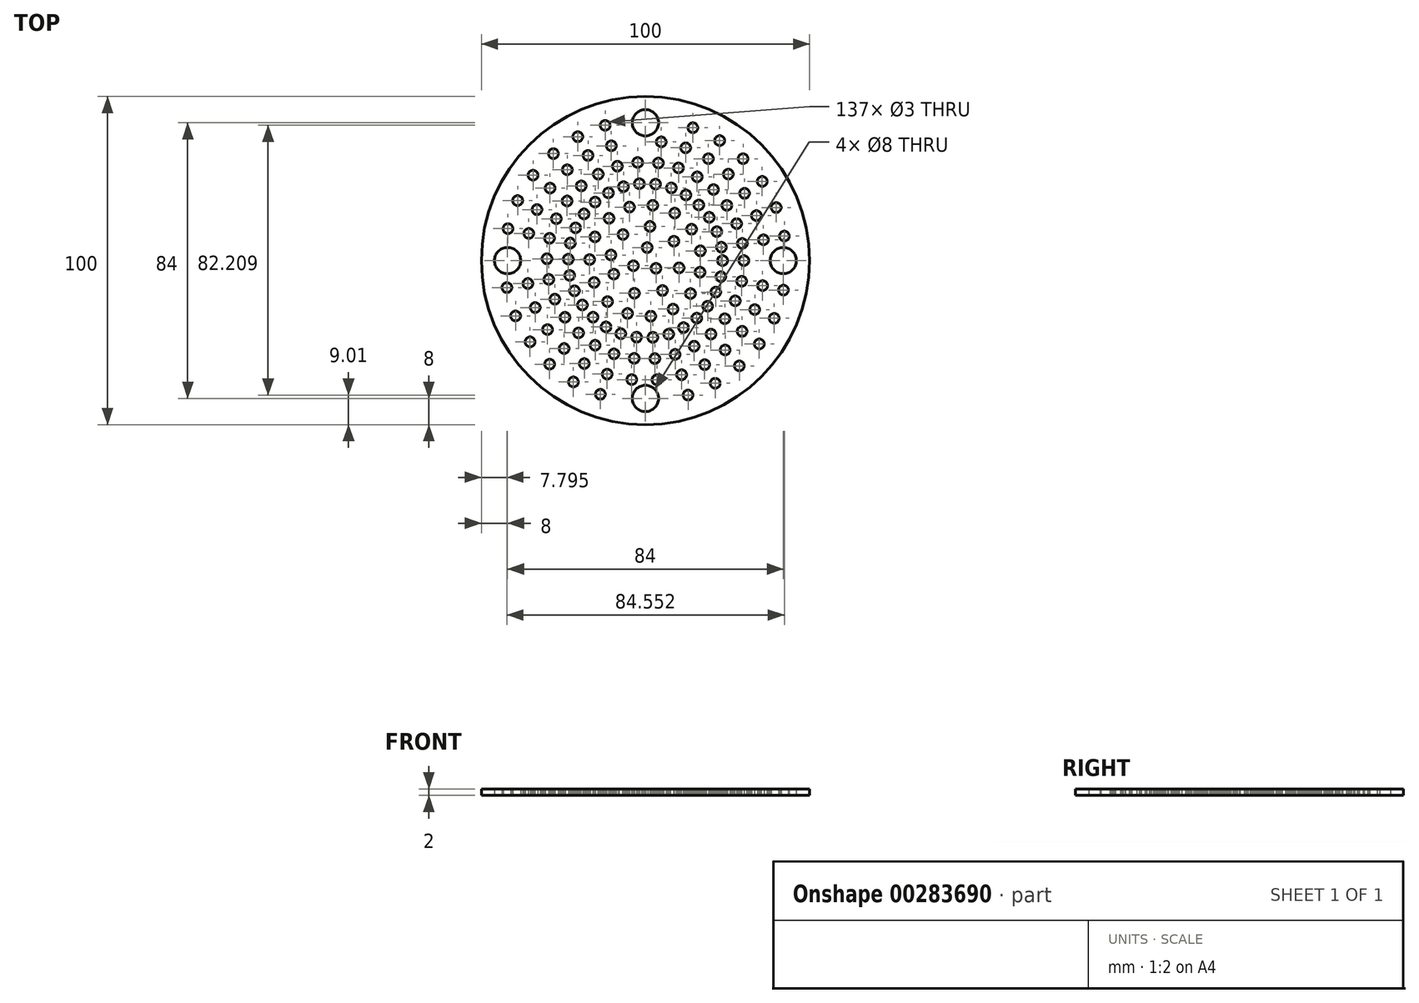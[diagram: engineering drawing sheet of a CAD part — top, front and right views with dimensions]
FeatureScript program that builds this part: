
annotation { "Feature Type Name" : "Feature", "Feature Type Description" : "" }
export const myFeature = defineFeature(function(context is Context, id is Id, definition is map)
    precondition{}
    {
        {
            var Q0;
            Q0=qCreatedBy(makeId("Top.planeOp"),FACE);
            var sketch = newSketch(context, id + "F0", { "sketchPlane" : qUnion([Q0])});
            skCircle(sketch, "E0", {"center": v(0, 0) * mm, "radius": 50 * mm});
            skCircle(sketch, "E1", {"center": v(-42, 0) * mm, "radius": 4 * mm});
            skCircle(sketch, "E2.1.0", {"center": v(0, 42) * mm, "radius": 4 * mm});
            skCircle(sketch, "E2.2.0", {"center": v(42, 0) * mm, "radius": 4 * mm});
            skCircle(sketch, "E2.3.0", {"center": v(0, -42) * mm, "radius": 4 * mm});
            skLineSegment(sketch, "E2.anchor1", {"start": v(0, 0) * mm, "end": v(-42, 0) * mm, "construction": true});
            skLineSegment(sketch, "E2.anchor2", {"start": v(0, 0) * mm, "end": v(0, -42) * mm, "construction": true});
            skCircle(sketch, "E3.3.0.0", {"center": v(23.5, 0) * mm, "radius": 1.5 * mm});
            skCircle(sketch, "E3.4.0.0", {"center": v(30, 0) * mm, "radius": 1.5 * mm});
            skLineSegment(sketch, "E3.direction1", {"start": v(4, 0) * mm, "end": v(10.5, 0) * mm, "construction": true});
            skLineSegment(sketch, "E3.direction2", {"start": v(4, 0) * mm, "end": v(4, 22) * mm, "construction": true});
            skCircle(sketch, "E4.1.0", {"center": v(35.7, -7.63) * mm, "radius": 1.5 * mm});
            skCircle(sketch, "E4.1.1", {"center": v(29.34, -6.27) * mm, "radius": 1.5 * mm});
            skCircle(sketch, "E4.1.2", {"center": v(22.98, -4.91) * mm, "radius": 1.5 * mm});
            skCircle(sketch, "E4.1.3", {"center": v(16.62, -3.55) * mm, "radius": 1.5 * mm});
            skCircle(sketch, "E4.1.4", {"center": v(10.27, -2.2) * mm, "radius": 1.5 * mm});
            skLineSegment(sketch, "E4.1.6", {"start": v(3.91, -0.84) * mm, "end": v(10.27, -2.2) * mm, "construction": true});
            skCircle(sketch, "E4.1.7", {"center": v(42.05, -9) * mm, "radius": 1.5 * mm});
            skCircle(sketch, "E4.2.0", {"center": v(33.3, -14.93) * mm, "radius": 1.5 * mm});
            skCircle(sketch, "E4.2.1", {"center": v(27.38, -12.27) * mm, "radius": 1.5 * mm});
            skCircle(sketch, "E4.2.2", {"center": v(21.45, -9.6) * mm, "radius": 1.5 * mm});
            skLineSegment(sketch, "E4.2.6", {"start": v(3.65, -1.64) * mm, "end": v(9.58, -4.3) * mm, "construction": true});
            skCircle(sketch, "E4.2.7", {"center": v(39.24, -17.58) * mm, "radius": 1.5 * mm});
            skCircle(sketch, "E4.3.0", {"center": v(29.45, -21.56) * mm, "radius": 1.5 * mm});
            skCircle(sketch, "E4.3.1", {"center": v(24.2, -17.72) * mm, "radius": 1.5 * mm});
            skCircle(sketch, "E4.3.2", {"center": v(18.96, -13.88) * mm, "radius": 1.5 * mm});
            skCircle(sketch, "E4.3.3", {"center": v(13.72, -10.04) * mm, "radius": 1.5 * mm});
            skCircle(sketch, "E4.3.5", {"center": v(3.23, -2.36) * mm, "radius": 1.5 * mm});
            skLineSegment(sketch, "E4.3.6", {"start": v(3.23, -2.36) * mm, "end": v(8.47, -6.2) * mm, "construction": true});
            skCircle(sketch, "E4.3.7", {"center": v(34.7, -25.4) * mm, "radius": 1.5 * mm});
            skCircle(sketch, "E4.4.0", {"center": v(24.3, -27.24) * mm, "radius": 1.5 * mm});
            skCircle(sketch, "E4.4.1", {"center": v(19.97, -22.4) * mm, "radius": 1.5 * mm});
            skCircle(sketch, "E4.4.2", {"center": v(15.64, -17.54) * mm, "radius": 1.5 * mm});
            skLineSegment(sketch, "E4.4.6", {"start": v(2.66, -2.99) * mm, "end": v(6.99, -7.84) * mm, "construction": true});
            skCircle(sketch, "E4.4.7", {"center": v(28.62, -32.1) * mm, "radius": 1.5 * mm});
            skCircle(sketch, "E4.5.0", {"center": v(18.06, -31.72) * mm, "radius": 1.5 * mm});
            skCircle(sketch, "E4.5.1", {"center": v(14.84, -26.07) * mm, "radius": 1.5 * mm});
            skCircle(sketch, "E4.5.2", {"center": v(11.63, -20.42) * mm, "radius": 1.5 * mm});
            skCircle(sketch, "E4.5.3", {"center": v(8.41, -14.77) * mm, "radius": 1.5 * mm});
            skCircle(sketch, "E4.5.4", {"center": v(5.2, -9.12) * mm, "radius": 1.5 * mm});
            skLineSegment(sketch, "E4.5.6", {"start": v(1.98, -3.48) * mm, "end": v(5.2, -9.12) * mm, "construction": true});
            skCircle(sketch, "E4.5.7", {"center": v(21.28, -37.37) * mm, "radius": 1.5 * mm});
            skCircle(sketch, "E4.6.0", {"center": v(11.03, -34.8) * mm, "radius": 1.5 * mm});
            skCircle(sketch, "E4.6.1", {"center": v(9.06, -28.6) * mm, "radius": 1.5 * mm});
            skCircle(sketch, "E4.6.2", {"center": v(7.1, -22.4) * mm, "radius": 1.5 * mm});
            skLineSegment(sketch, "E4.6.6", {"start": v(1.2, -3.81) * mm, "end": v(3.17, -10) * mm, "construction": true});
            skCircle(sketch, "E4.6.7", {"center": v(13, -41) * mm, "radius": 1.5 * mm});
            skCircle(sketch, "E4.7.0", {"center": v(3.5, -36.33) * mm, "radius": 1.5 * mm});
            skCircle(sketch, "E4.7.1", {"center": v(2.88, -29.86) * mm, "radius": 1.5 * mm});
            skCircle(sketch, "E4.7.2", {"center": v(2.26, -23.4) * mm, "radius": 1.5 * mm});
            skCircle(sketch, "E4.7.3", {"center": v(1.63, -16.92) * mm, "radius": 1.5 * mm});
            skLineSegment(sketch, "E4.7.6", {"start": v(0.38, -3.98) * mm, "end": v(1, -10.45) * mm, "construction": true});
            skCircle(sketch, "E4.8.0", {"center": v(-4.16, -36.26) * mm, "radius": 1.5 * mm});
            skCircle(sketch, "E4.8.1", {"center": v(-3.42, -29.8) * mm, "radius": 1.5 * mm});
            skCircle(sketch, "E4.8.2", {"center": v(-2.68, -23.35) * mm, "radius": 1.5 * mm});
            skLineSegment(sketch, "E4.8.6", {"start": v(-0.46, -3.97) * mm, "end": v(-1.2, -10.43) * mm, "construction": true});
            skCircle(sketch, "E4.9.0", {"center": v(-11.65, -34.59) * mm, "radius": 1.5 * mm});
            skCircle(sketch, "E4.9.1", {"center": v(-9.58, -28.43) * mm, "radius": 1.5 * mm});
            skCircle(sketch, "E4.9.2", {"center": v(-7.5, -22.27) * mm, "radius": 1.5 * mm});
            skCircle(sketch, "E4.9.3", {"center": v(-5.43, -16.11) * mm, "radius": 1.5 * mm});
            skCircle(sketch, "E4.9.4", {"center": v(-3.35, -9.95) * mm, "radius": 1.5 * mm});
            skLineSegment(sketch, "E4.9.6", {"start": v(-1.28, -3.8) * mm, "end": v(-3.35, -9.95) * mm, "construction": true});
            skCircle(sketch, "E4.9.7", {"center": v(-13.73, -40.75) * mm, "radius": 1.5 * mm});
            skCircle(sketch, "E4.10.0", {"center": v(-18.63, -31.39) * mm, "radius": 1.5 * mm});
            skCircle(sketch, "E4.10.1", {"center": v(-15.31, -25.8) * mm, "radius": 1.5 * mm});
            skCircle(sketch, "E4.10.2", {"center": v(-12, -20.2) * mm, "radius": 1.5 * mm});
            skLineSegment(sketch, "E4.10.6", {"start": v(-2.04, -3.44) * mm, "end": v(-5.36, -9.03) * mm, "construction": true});
            skCircle(sketch, "E4.10.7", {"center": v(-21.95, -36.98) * mm, "radius": 1.5 * mm});
            skCircle(sketch, "E4.11.0", {"center": v(-24.78, -26.8) * mm, "radius": 1.5 * mm});
            skCircle(sketch, "E4.11.1", {"center": v(-20.37, -22.03) * mm, "radius": 1.5 * mm});
            skCircle(sketch, "E4.11.2", {"center": v(-15.95, -17.25) * mm, "radius": 1.5 * mm});
            skCircle(sketch, "E4.11.3", {"center": v(-11.54, -12.48) * mm, "radius": 1.5 * mm});
            skLineSegment(sketch, "E4.11.6", {"start": v(-2.72, -2.94) * mm, "end": v(-7.13, -7.7) * mm, "construction": true});
            skCircle(sketch, "E4.11.7", {"center": v(-29.2, -31.57) * mm, "radius": 1.5 * mm});
            skCircle(sketch, "E4.12.0", {"center": v(-29.84, -21.03) * mm, "radius": 1.5 * mm});
            skCircle(sketch, "E4.12.1", {"center": v(-24.52, -17.28) * mm, "radius": 1.5 * mm});
            skCircle(sketch, "E4.12.2", {"center": v(-19.2, -13.54) * mm, "radius": 1.5 * mm});
            skLineSegment(sketch, "E4.12.6", {"start": v(-3.27, -2.3) * mm, "end": v(-8.58, -6.05) * mm, "construction": true});
            skCircle(sketch, "E4.12.7", {"center": v(-35.15, -24.77) * mm, "radius": 1.5 * mm});
            skCircle(sketch, "E4.13.0", {"center": v(-33.57, -14.32) * mm, "radius": 1.5 * mm});
            skCircle(sketch, "E4.13.1", {"center": v(-27.6, -11.77) * mm, "radius": 1.5 * mm});
            skCircle(sketch, "E4.13.2", {"center": v(-21.62, -9.22) * mm, "radius": 1.5 * mm});
            skCircle(sketch, "E4.13.3", {"center": v(-15.64, -6.67) * mm, "radius": 1.5 * mm});
            skCircle(sketch, "E4.13.4", {"center": v(-9.66, -4.12) * mm, "radius": 1.5 * mm});
            skCircle(sketch, "E4.13.5", {"center": v(-3.68, -1.57) * mm, "radius": 1.5 * mm});
            skLineSegment(sketch, "E4.13.6", {"start": v(-3.68, -1.57) * mm, "end": v(-9.66, -4.12) * mm, "construction": true});
            skCircle(sketch, "E4.13.7", {"center": v(-39.55, -16.87) * mm, "radius": 1.5 * mm});
            skCircle(sketch, "E4.14.0", {"center": v(-35.83, -6.99) * mm, "radius": 1.5 * mm});
            skCircle(sketch, "E4.14.1", {"center": v(-29.45, -5.74) * mm, "radius": 1.5 * mm});
            skCircle(sketch, "E4.14.2", {"center": v(-23.07, -4.5) * mm, "radius": 1.5 * mm});
            skLineSegment(sketch, "E4.14.6", {"start": v(-3.93, -0.77) * mm, "end": v(-10.3, -2) * mm, "construction": true});
            skCircle(sketch, "E4.14.7", {"center": v(-42.2, -8.23) * mm, "radius": 1.5 * mm});
            skCircle(sketch, "E4.15.1", {"center": v(-30, 0.54) * mm, "radius": 1.5 * mm});
            skCircle(sketch, "E4.15.2", {"center": v(-23.5, 0.42) * mm, "radius": 1.5 * mm});
            skCircle(sketch, "E4.15.3", {"center": v(-17, 0.3) * mm, "radius": 1.5 * mm});
            skCircle(sketch, "E4.15.4", {"center": v(-10.5, 1.69) * mm, "radius": 1.5 * mm});
            skLineSegment(sketch, "E4.15.6", {"start": v(-4, 0.07) * mm, "end": v(-10.5, 0.19) * mm, "construction": true});
            skCircle(sketch, "E4.16.0", {"center": v(-35.55, 8.27) * mm, "radius": 1.5 * mm});
            skCircle(sketch, "E4.16.1", {"center": v(-29.22, 6.8) * mm, "radius": 1.5 * mm});
            skCircle(sketch, "E4.16.2", {"center": v(-22.89, 5.33) * mm, "radius": 1.5 * mm});
            skLineSegment(sketch, "E4.16.6", {"start": v(-3.9, 0.9) * mm, "end": v(-10.23, 2.38) * mm, "construction": true});
            skCircle(sketch, "E4.16.7", {"center": v(-41.88, 9.75) * mm, "radius": 1.5 * mm});
            skCircle(sketch, "E4.17.0", {"center": v(-33.03, 15.53) * mm, "radius": 1.5 * mm});
            skCircle(sketch, "E4.17.1", {"center": v(-27.15, 12.76) * mm, "radius": 1.5 * mm});
            skCircle(sketch, "E4.17.2", {"center": v(-21.27, 10) * mm, "radius": 1.5 * mm});
            skCircle(sketch, "E4.17.3", {"center": v(-15.39, 7.23) * mm, "radius": 1.5 * mm});
            skLineSegment(sketch, "E4.17.6", {"start": v(-3.62, 1.7) * mm, "end": v(-9.5, 4.47) * mm, "construction": true});
            skCircle(sketch, "E4.17.7", {"center": v(-38.92, 18.29) * mm, "radius": 1.5 * mm});
            skCircle(sketch, "E4.18.0", {"center": v(-29.06, 22.09) * mm, "radius": 1.5 * mm});
            skCircle(sketch, "E4.18.1", {"center": v(-23.88, 18.16) * mm, "radius": 1.5 * mm});
            skCircle(sketch, "E4.18.2", {"center": v(-18.7, 14.22) * mm, "radius": 1.5 * mm});
            skLineSegment(sketch, "E4.18.6", {"start": v(-3.18, 2.42) * mm, "end": v(-8.36, 6.35) * mm, "construction": true});
            skCircle(sketch, "E4.18.7", {"center": v(-34.23, 26.02) * mm, "radius": 1.5 * mm});
            skCircle(sketch, "E4.19.0", {"center": v(-23.8, 27.68) * mm, "radius": 1.5 * mm});
            skCircle(sketch, "E4.19.1", {"center": v(-19.56, 22.75) * mm, "radius": 1.5 * mm});
            skCircle(sketch, "E4.19.2", {"center": v(-15.32, 17.82) * mm, "radius": 1.5 * mm});
            skCircle(sketch, "E4.19.3", {"center": v(-11.08, 12.9) * mm, "radius": 1.5 * mm});
            skCircle(sketch, "E4.19.4", {"center": v(-6.85, 7.96) * mm, "radius": 1.5 * mm});
            skLineSegment(sketch, "E4.19.6", {"start": v(-2.6, 3.03) * mm, "end": v(-6.85, 7.96) * mm, "construction": true});
            skCircle(sketch, "E4.19.7", {"center": v(-28.03, 32.6) * mm, "radius": 1.5 * mm});
            skCircle(sketch, "E4.20.0", {"center": v(-17.48, 32.04) * mm, "radius": 1.5 * mm});
            skCircle(sketch, "E4.20.1", {"center": v(-14.37, 26.33) * mm, "radius": 1.5 * mm});
            skCircle(sketch, "E4.20.2", {"center": v(-11.26, 20.63) * mm, "radius": 1.5 * mm});
            skLineSegment(sketch, "E4.20.6", {"start": v(-1.92, 3.51) * mm, "end": v(-5.03, 9.22) * mm, "construction": true});
            skCircle(sketch, "E4.20.7", {"center": v(-20.6, 37.75) * mm, "radius": 1.5 * mm});
            skCircle(sketch, "E4.21.0", {"center": v(-10.4, 34.99) * mm, "radius": 1.5 * mm});
            skCircle(sketch, "E4.21.1", {"center": v(-8.55, 28.76) * mm, "radius": 1.5 * mm});
            skCircle(sketch, "E4.21.2", {"center": v(-6.7, 22.53) * mm, "radius": 1.5 * mm});
            skCircle(sketch, "E4.21.3", {"center": v(-4.84, 16.3) * mm, "radius": 1.5 * mm});
            skLineSegment(sketch, "E4.21.6", {"start": v(-1.14, 3.83) * mm, "end": v(-3, 10.06) * mm, "construction": true});
            skCircle(sketch, "E4.21.7", {"center": v(-12.25, 41.22) * mm, "radius": 1.5 * mm});
            skCircle(sketch, "E4.22.1", {"center": v(-2.34, 29.9) * mm, "radius": 1.5 * mm});
            skCircle(sketch, "E4.22.2", {"center": v(-1.84, 23.43) * mm, "radius": 1.5 * mm});
            skLineSegment(sketch, "E4.22.6", {"start": v(-0.31, 3.99) * mm, "end": v(-0.82, 10.47) * mm, "construction": true});
            skCircle(sketch, "E4.23.0", {"center": v(4.82, 36.18) * mm, "radius": 1.5 * mm});
            skCircle(sketch, "E4.23.1", {"center": v(3.96, 29.74) * mm, "radius": 1.5 * mm});
            skCircle(sketch, "E4.23.2", {"center": v(3.1, 23.3) * mm, "radius": 1.5 * mm});
            skCircle(sketch, "E4.23.3", {"center": v(2.24, 16.85) * mm, "radius": 1.5 * mm});
            skCircle(sketch, "E4.23.4", {"center": v(1.39, 10.4) * mm, "radius": 1.5 * mm});
            skCircle(sketch, "E4.23.5", {"center": v(0.53, 3.96) * mm, "radius": 1.5 * mm});
            skLineSegment(sketch, "E4.23.6", {"start": v(0.53, 3.96) * mm, "end": v(1.39, 10.4) * mm, "construction": true});
            skCircle(sketch, "E4.24.0", {"center": v(12.28, 34.37) * mm, "radius": 1.5 * mm});
            skCircle(sketch, "E4.24.1", {"center": v(10.1, 28.25) * mm, "radius": 1.5 * mm});
            skCircle(sketch, "E4.24.2", {"center": v(7.9, 22.13) * mm, "radius": 1.5 * mm});
            skLineSegment(sketch, "E4.24.6", {"start": v(1.35, 3.77) * mm, "end": v(3.53, 9.89) * mm, "construction": true});
            skCircle(sketch, "E4.24.7", {"center": v(14.46, 40.5) * mm, "radius": 1.5 * mm});
            skCircle(sketch, "E4.25.0", {"center": v(19.2, 31.05) * mm, "radius": 1.5 * mm});
            skCircle(sketch, "E4.25.1", {"center": v(15.77, 25.52) * mm, "radius": 1.5 * mm});
            skCircle(sketch, "E4.25.2", {"center": v(12.36, 19.99) * mm, "radius": 1.5 * mm});
            skCircle(sketch, "E4.25.3", {"center": v(8.94, 14.46) * mm, "radius": 1.5 * mm});
            skLineSegment(sketch, "E4.25.6", {"start": v(2.1, 3.4) * mm, "end": v(5.52, 8.93) * mm, "construction": true});
            skCircle(sketch, "E4.25.7", {"center": v(22.61, 36.58) * mm, "radius": 1.5 * mm});
            skCircle(sketch, "E4.26.0", {"center": v(25.26, 26.35) * mm, "radius": 1.5 * mm});
            skCircle(sketch, "E4.26.1", {"center": v(20.76, 21.66) * mm, "radius": 1.5 * mm});
            skCircle(sketch, "E4.26.2", {"center": v(16.26, 16.96) * mm, "radius": 1.5 * mm});
            skLineSegment(sketch, "E4.26.6", {"start": v(2.77, 2.89) * mm, "end": v(7.27, 7.58) * mm, "construction": true});
            skCircle(sketch, "E4.26.7", {"center": v(29.76, 31.04) * mm, "radius": 1.5 * mm});
            skCircle(sketch, "E4.27.0", {"center": v(30.21, 20.48) * mm, "radius": 1.5 * mm});
            skCircle(sketch, "E4.27.1", {"center": v(24.83, 16.84) * mm, "radius": 1.5 * mm});
            skCircle(sketch, "E4.27.2", {"center": v(19.45, 13.19) * mm, "radius": 1.5 * mm});
            skCircle(sketch, "E4.27.3", {"center": v(14.07, 9.54) * mm, "radius": 1.5 * mm});
            skCircle(sketch, "E4.27.4", {"center": v(8.7, 5.9) * mm, "radius": 1.5 * mm});
            skLineSegment(sketch, "E4.27.6", {"start": v(3.31, 2.24) * mm, "end": v(8.7, 5.9) * mm, "construction": true});
            skCircle(sketch, "E4.27.7", {"center": v(35.6, 24.13) * mm, "radius": 1.5 * mm});
            skCircle(sketch, "E4.28.0", {"center": v(33.83, 13.71) * mm, "radius": 1.5 * mm});
            skCircle(sketch, "E4.28.1", {"center": v(27.8, 11.27) * mm, "radius": 1.5 * mm});
            skCircle(sketch, "E4.28.2", {"center": v(21.78, 8.83) * mm, "radius": 1.5 * mm});
            skLineSegment(sketch, "E4.28.6", {"start": v(3.7, 1.5) * mm, "end": v(9.73, 3.95) * mm, "construction": true});
            skCircle(sketch, "E4.28.7", {"center": v(39.85, 16.16) * mm, "radius": 1.5 * mm});
            skCircle(sketch, "E4.29.0", {"center": v(35.95, 6.34) * mm, "radius": 1.5 * mm});
            skCircle(sketch, "E4.29.1", {"center": v(29.54, 5.2) * mm, "radius": 1.5 * mm});
            skCircle(sketch, "E4.29.2", {"center": v(23.14, 4.08) * mm, "radius": 1.5 * mm});
            skCircle(sketch, "E4.29.3", {"center": v(16.74, 2.95) * mm, "radius": 1.5 * mm});
            skLineSegment(sketch, "E4.29.6", {"start": v(3.94, 0.7) * mm, "end": v(10.34, 1.82) * mm, "construction": true});
            skCircle(sketch, "E4.29.7", {"center": v(42.35, 7.47) * mm, "radius": 1.5 * mm});
            skLineSegment(sketch, "E4.anchor1", {"start": v(0, 0) * mm, "end": v(4, 0) * mm, "construction": true});
            skLineSegment(sketch, "E4.anchor2", {"start": v(0, 0) * mm, "end": v(3.94, 0.7) * mm, "construction": true});
            skSolve(sketch);
        }
        {
            var Q0;
            Q0=makeQuery(id+"F0.imprint","IMPRINT",FACE,{"disambiguationData":[TD([[makeQuery(id+"F0.imprint","IMPRINT",EDGE,{"derivedFrom":sQuery(id+"F0.wireOp",EDGE,"E0")}),1.0]])]});
            extrude(context, id + "F1", {"entities" : qUnion([Q0]), "depth" : 2 * mm});
        }
    });
